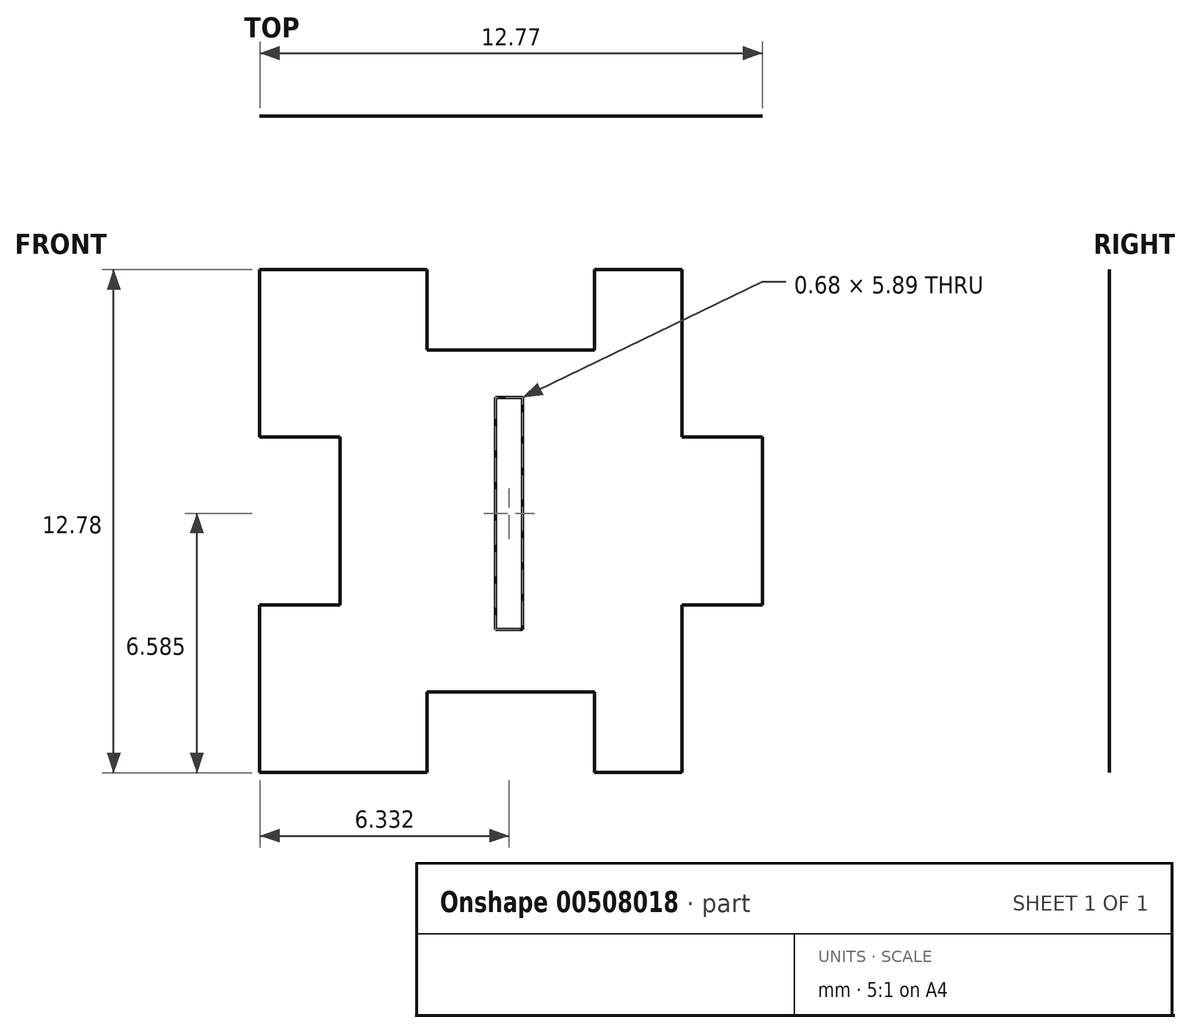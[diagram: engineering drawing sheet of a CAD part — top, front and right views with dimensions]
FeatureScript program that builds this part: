
annotation { "Feature Type Name" : "Feature", "Feature Type Description" : "" }
export const myFeature = defineFeature(function(context is Context, id is Id, definition is map)
    precondition{}
    {
        {
            var Q0;
            Q0=qCreatedBy(makeId("Front.planeOp"),FACE);
            var sketch = newSketch(context, id + "F0", { "sketchPlane" : qUnion([Q0])});
            skLineSegment(sketch, "E0", {"start": v(-10.99, 26.89) * mm, "end": v(-10.99, 29.02) * mm});
            skLineSegment(sketch, "E1", {"start": v(-10.99, 29.02) * mm, "end": v(-13.03, 29.02) * mm});
            skLineSegment(sketch, "E2", {"start": v(-13.03, 29.02) * mm, "end": v(-13.03, 33.28) * mm});
            skLineSegment(sketch, "E3", {"start": v(-13.03, 33.28) * mm, "end": v(-8.78, 33.28) * mm});
            skLineSegment(sketch, "E4", {"start": v(-8.78, 33.28) * mm, "end": v(-8.78, 31.23) * mm});
            skLineSegment(sketch, "E5", {"start": v(-8.78, 31.23) * mm, "end": v(-4.53, 31.23) * mm});
            skLineSegment(sketch, "E6", {"start": v(-4.53, 31.23) * mm, "end": v(-4.53, 33.28) * mm});
            skLineSegment(sketch, "E7", {"start": v(-4.53, 33.28) * mm, "end": v(-2.3, 33.28) * mm});
            skLineSegment(sketch, "E8", {"start": v(-2.3, 33.28) * mm, "end": v(-2.3, 29.02) * mm});
            skLineSegment(sketch, "E9", {"start": v(-2.3, 29.02) * mm, "end": v(-0.26, 29.02) * mm});
            skLineSegment(sketch, "E10", {"start": v(-10.99, 26.89) * mm, "end": v(8.72, 26.89) * mm, "construction": true});
            skLineSegment(sketch, "E11.MirrorCS", {"start": v(-2.3, 24.76) * mm, "end": v(-0.26, 24.76) * mm});
            skLineSegment(sketch, "E12.MirrorCS", {"start": v(-2.3, 20.5) * mm, "end": v(-2.3, 24.76) * mm});
            skLineSegment(sketch, "E13.MirrorCS", {"start": v(-4.53, 20.5) * mm, "end": v(-2.3, 20.5) * mm});
            skLineSegment(sketch, "E14.MirrorCS", {"start": v(-4.53, 22.55) * mm, "end": v(-4.53, 20.5) * mm});
            skLineSegment(sketch, "E15.MirrorCS", {"start": v(-8.78, 22.55) * mm, "end": v(-4.53, 22.55) * mm});
            skLineSegment(sketch, "E16.MirrorCS", {"start": v(-8.78, 20.5) * mm, "end": v(-8.78, 22.55) * mm});
            skLineSegment(sketch, "E17.MirrorCS", {"start": v(-13.03, 20.5) * mm, "end": v(-8.78, 20.5) * mm});
            skLineSegment(sketch, "E18.MirrorCS", {"start": v(-13.03, 24.76) * mm, "end": v(-13.03, 20.5) * mm});
            skLineSegment(sketch, "E19.MirrorCS", {"start": v(-10.99, 24.76) * mm, "end": v(-13.03, 24.76) * mm});
            skLineSegment(sketch, "E20.MirrorCS", {"start": v(-10.99, 26.89) * mm, "end": v(-10.99, 24.76) * mm});
            skLineSegment(sketch, "E21", {"start": v(-0.26, 29.02) * mm, "end": v(-0.26, 24.76) * mm});
            skSolve(sketch);
        }
        {
            var Q0;
            Q0=makeQuery(id+"F0.imprint","IMPRINT",FACE,{"disambiguationData":[TD([[makeQuery(id+"F0.imprint","IMPRINT",EDGE,{"derivedFrom":sQuery(id+"F0.wireOp",EDGE,"E0")}),-1.0]])]});
            extrude(context, id + "F1", {"entities" : qUnion([Q0]), "depth" : .16 / 50.8 * mm, "offsetDistance" : 25 * mm});
        }
        {
            var Q0;
            Q0=makeQuery(id+"F1.opExtrude","CAP_FACE",FACE,{"disambiguationData":[OSD([sQuery(id+"F0.wireOp",EDGE,"E0"),sQuery(id+"F0.wireOp",EDGE,"E1"),sQuery(id+"F0.wireOp",EDGE,"E2"),sQuery(id+"F0.wireOp",EDGE,"E3"),sQuery(id+"F0.wireOp",EDGE,"E4"),sQuery(id+"F0.wireOp",EDGE,"E5"),sQuery(id+"F0.wireOp",EDGE,"E6"),sQuery(id+"F0.wireOp",EDGE,"E7"),sQuery(id+"F0.wireOp",EDGE,"E8"),sQuery(id+"F0.wireOp",EDGE,"E9"),sQuery(id+"F0.wireOp",EDGE,"E11.MirrorCS"),sQuery(id+"F0.wireOp",EDGE,"E12.MirrorCS"),sQuery(id+"F0.wireOp",EDGE,"E13.MirrorCS"),sQuery(id+"F0.wireOp",EDGE,"E14.MirrorCS"),sQuery(id+"F0.wireOp",EDGE,"E15.MirrorCS"),sQuery(id+"F0.wireOp",EDGE,"E16.MirrorCS"),sQuery(id+"F0.wireOp",EDGE,"E17.MirrorCS"),sQuery(id+"F0.wireOp",EDGE,"E18.MirrorCS"),sQuery(id+"F0.wireOp",EDGE,"E19.MirrorCS"),sQuery(id+"F0.wireOp",EDGE,"E20.MirrorCS"),sQuery(id+"F0.wireOp",EDGE,"E21")])],"isStart":false});
            var sketch = newSketch(context, id + "F2", { "sketchPlane" : qUnion([Q0])});
            skText(sketch, "E22", { "text": "I", "fontName": "OpenSans-Regular.ttf"});
            const initialGuessF2  = {"E22": [-0.00785, 0.02414, 1, 0, 0.00594]};
            skSetInitialGuess(sketch, initialGuessF2);
            skSolve(sketch);
        }
        {
            var Q0;
            Q0=makeQuery(id+"F2.imprint","IMPRINT",FACE,{"disambiguationData":[TD([[makeQuery(id+"F2.imprint","IMPRINT",EDGE,{"derivedFrom":sQuery(id+"F2.wireOp",EDGE,"E22.sketch_text.stroke-0")}),-1.0]])]});
            extrude(context, id + "F3", {"entities" : qUnion([Q0]), "operationType" : NewBodyOperationType.REMOVE, "oppositeDirection" : true, "depth" : 1 * mm, "offsetDistance" : 25 * mm});
        }
    });
